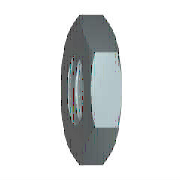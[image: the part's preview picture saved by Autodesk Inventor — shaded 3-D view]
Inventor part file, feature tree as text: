
AUTODESK INVENTOR PART (.ipt)
format: ipt  version: 2022 (Build 260153000, 153)  size: 176,640 bytes
history: native  units: mm (DEFAULTED — no unit token found)
features: sketch x3, other x2, extrude x1, hole x1, plane x1
ambient origin geometry x7: Origin, YZ Plane, XZ Plane, X Axis, Y Axis, Z Axis, Center Point
bodies: Solid1 (feature_tree)
feature tree (8):
  extrude  "Базовый элемент"  Depth=9.237604mm
  other  "Фаска1"
  hole  "Резьба"  [1 undecoded]
  other  "Work Axis1"
  plane  "Work Plane1"
  sketch  "Эскиз1"
  sketch  "Эскиз2"
  sketch  "Эскиз3"
note: 1 required parameter value undecoded (feature->parameter linkage not recoverable at this tier; creation-order binding heuristic only, values carry confidence <= 0.55)
